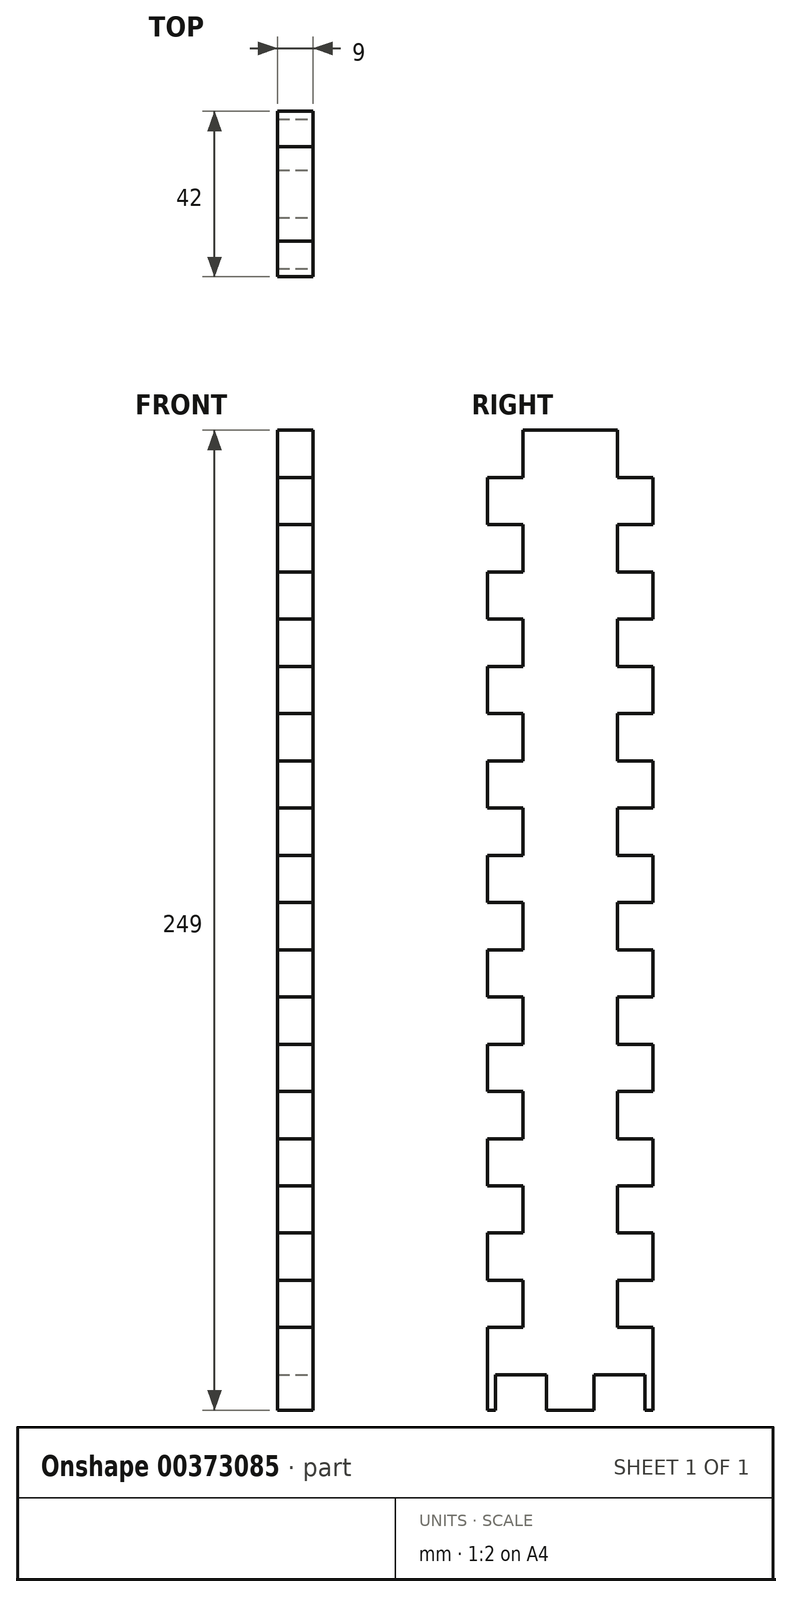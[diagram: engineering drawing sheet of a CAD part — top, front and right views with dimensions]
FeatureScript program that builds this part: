
annotation { "Feature Type Name" : "Feature", "Feature Type Description" : "" }
export const myFeature = defineFeature(function(context is Context, id is Id, definition is map)
    precondition{}
    {
        {
            var Q0;
            Q0=qCreatedBy(makeId("Right.planeOp"),FACE);
            var sketch = newSketch(context, id + "F0", { "sketchPlane" : qUnion([Q0])});
            skLineSegment(sketch, "E0.bottom", {"start": v(-12, 120) * mm, "end": v(12, 120) * mm});
            skLineSegment(sketch, "E0.top", {"start": v(-12, -120) * mm, "end": v(12, -120) * mm});
            skLineSegment(sketch, "E0.left", {"start": v(-12, 120) * mm, "end": v(-12, -120) * mm});
            skLineSegment(sketch, "E0.right", {"start": v(12, 120) * mm, "end": v(12, -120) * mm});
            skPoint(sketch, "E0.middle", {"position": v(0, 0) * mm});
            skSolve(sketch);
        }
        {
            var Q0;
            Q0=makeQuery(id+"F0.imprint","IMPRINT",FACE,{"disambiguationData":[TD([[makeQuery(id+"F0.imprint","IMPRINT",EDGE,{"derivedFrom":sQuery(id+"F0.wireOp",EDGE,"E0.bottom")}),-1.0]])]});
            extrude(context, id + "F1", {"entities" : qUnion([Q0]), "depth" : 9 * mm});
        }
        {
            var Q0;
            Q0=makeQuery(id+"F1.opExtrude","CAP_FACE",FACE,{"disambiguationData":[OSD([sQuery(id+"F0.wireOp",EDGE,"E0.bottom"),sQuery(id+"F0.wireOp",EDGE,"E0.top"),sQuery(id+"F0.wireOp",EDGE,"E0.left"),sQuery(id+"F0.wireOp",EDGE,"E0.right")])],"isStart":false});
            var sketch = newSketch(context, id + "F2", { "sketchPlane" : qUnion([Q0])});
            skLineSegment(sketch, "E1.bottom", {"start": v(-12, -120) * mm, "end": v(-21, -120) * mm});
            skLineSegment(sketch, "E1.top", {"start": v(-12, -108) * mm, "end": v(-21, -108) * mm});
            skLineSegment(sketch, "E1.left", {"start": v(-12, -120) * mm, "end": v(-12, -108) * mm});
            skLineSegment(sketch, "E1.right", {"start": v(-21, -120) * mm, "end": v(-21, -108) * mm});
            skLineSegment(sketch, "E2.0.1.0", {"start": v(-12, -84) * mm, "end": v(-21, -84) * mm});
            skLineSegment(sketch, "E2.0.1.1", {"start": v(-12, -96) * mm, "end": v(-12, -84) * mm});
            skLineSegment(sketch, "E2.0.1.2", {"start": v(-12, -96) * mm, "end": v(-21, -96) * mm});
            skLineSegment(sketch, "E2.0.1.3", {"start": v(-21, -96) * mm, "end": v(-21, -84) * mm});
            skLineSegment(sketch, "E2.0.2.0", {"start": v(-12, -60) * mm, "end": v(-21, -60) * mm});
            skLineSegment(sketch, "E2.0.2.1", {"start": v(-12, -72) * mm, "end": v(-12, -60) * mm});
            skLineSegment(sketch, "E2.0.2.2", {"start": v(-12, -72) * mm, "end": v(-21, -72) * mm});
            skLineSegment(sketch, "E2.0.2.3", {"start": v(-21, -72) * mm, "end": v(-21, -60) * mm});
            skLineSegment(sketch, "E2.0.3.0", {"start": v(-12, -36) * mm, "end": v(-21, -36) * mm});
            skLineSegment(sketch, "E2.0.3.1", {"start": v(-12, -48) * mm, "end": v(-12, -36) * mm});
            skLineSegment(sketch, "E2.0.3.2", {"start": v(-12, -48) * mm, "end": v(-21, -48) * mm});
            skLineSegment(sketch, "E2.0.3.3", {"start": v(-21, -48) * mm, "end": v(-21, -36) * mm});
            skLineSegment(sketch, "E2.0.4.0", {"start": v(-12, -12) * mm, "end": v(-21, -12) * mm});
            skLineSegment(sketch, "E2.0.4.1", {"start": v(-12, -24) * mm, "end": v(-12, -12) * mm});
            skLineSegment(sketch, "E2.0.4.2", {"start": v(-12, -24) * mm, "end": v(-21, -24) * mm});
            skLineSegment(sketch, "E2.0.4.3", {"start": v(-21, -24) * mm, "end": v(-21, -12) * mm});
            skLineSegment(sketch, "E2.0.5.0", {"start": v(-12, 12) * mm, "end": v(-21, 12) * mm});
            skLineSegment(sketch, "E2.0.5.1", {"start": v(-12, 0) * mm, "end": v(-12, 12) * mm});
            skLineSegment(sketch, "E2.0.5.2", {"start": v(-12, 0) * mm, "end": v(-21, 0) * mm});
            skLineSegment(sketch, "E2.0.5.3", {"start": v(-21, 0) * mm, "end": v(-21, 12) * mm});
            skLineSegment(sketch, "E2.0.6.0", {"start": v(-12, 36) * mm, "end": v(-21, 36) * mm});
            skLineSegment(sketch, "E2.0.6.1", {"start": v(-12, 24) * mm, "end": v(-12, 36) * mm});
            skLineSegment(sketch, "E2.0.6.2", {"start": v(-12, 24) * mm, "end": v(-21, 24) * mm});
            skLineSegment(sketch, "E2.0.6.3", {"start": v(-21, 24) * mm, "end": v(-21, 36) * mm});
            skLineSegment(sketch, "E2.0.7.0", {"start": v(-12, 60) * mm, "end": v(-21, 60) * mm});
            skLineSegment(sketch, "E2.0.7.1", {"start": v(-12, 48) * mm, "end": v(-12, 60) * mm});
            skLineSegment(sketch, "E2.0.7.2", {"start": v(-12, 48) * mm, "end": v(-21, 48) * mm});
            skLineSegment(sketch, "E2.0.7.3", {"start": v(-21, 48) * mm, "end": v(-21, 60) * mm});
            skLineSegment(sketch, "E2.0.8.0", {"start": v(-12, 84) * mm, "end": v(-21, 84) * mm});
            skLineSegment(sketch, "E2.0.8.1", {"start": v(-12, 72) * mm, "end": v(-12, 84) * mm});
            skLineSegment(sketch, "E2.0.8.2", {"start": v(-12, 72) * mm, "end": v(-21, 72) * mm});
            skLineSegment(sketch, "E2.0.8.3", {"start": v(-21, 72) * mm, "end": v(-21, 84) * mm});
            skLineSegment(sketch, "E2.0.9.0", {"start": v(-12, 108) * mm, "end": v(-21, 108) * mm});
            skLineSegment(sketch, "E2.0.9.1", {"start": v(-12, 96) * mm, "end": v(-12, 108) * mm});
            skLineSegment(sketch, "E2.0.9.2", {"start": v(-12, 96) * mm, "end": v(-21, 96) * mm});
            skLineSegment(sketch, "E2.0.9.3", {"start": v(-21, 96) * mm, "end": v(-21, 108) * mm});
            skLineSegment(sketch, "E2.direction1", {"start": v(-21, -108) * mm, "end": v(-11, -108) * mm, "construction": true});
            skLineSegment(sketch, "E2.direction2", {"start": v(-21, -108) * mm, "end": v(-21, -84) * mm, "construction": true});
            skLineSegment(sketch, "E3", {"start": v(0, 120) * mm, "end": v(0, 0) * mm});
            skLineSegment(sketch, "E4.MirrorCS", {"start": v(21, -96) * mm, "end": v(21, -84) * mm});
            skLineSegment(sketch, "E5.MirrorCS", {"start": v(21, 24) * mm, "end": v(21, 36) * mm});
            skLineSegment(sketch, "E6.MirrorCS", {"start": v(21, 96) * mm, "end": v(21, 108) * mm});
            skLineSegment(sketch, "E7.MirrorCS", {"start": v(21, -24) * mm, "end": v(21, -12) * mm});
            skLineSegment(sketch, "E8.MirrorCS", {"start": v(21, 72) * mm, "end": v(21, 84) * mm});
            skLineSegment(sketch, "E9.MirrorCS", {"start": v(12, 24) * mm, "end": v(21, 24) * mm});
            skLineSegment(sketch, "E10.MirrorCS", {"start": v(12, -24) * mm, "end": v(21, -24) * mm});
            skLineSegment(sketch, "E11.MirrorCS", {"start": v(12, 72) * mm, "end": v(21, 72) * mm});
            skLineSegment(sketch, "E12.MirrorCS", {"start": v(12, 0) * mm, "end": v(21, 0) * mm});
            skLineSegment(sketch, "E13.MirrorCS", {"start": v(21, 48) * mm, "end": v(21, 60) * mm});
            skLineSegment(sketch, "E14.MirrorCS", {"start": v(12, 96) * mm, "end": v(21, 96) * mm});
            skLineSegment(sketch, "E15.MirrorCS", {"start": v(12, -36) * mm, "end": v(21, -36) * mm});
            skLineSegment(sketch, "E16.MirrorCS", {"start": v(12, 24) * mm, "end": v(12, 36) * mm});
            skLineSegment(sketch, "E17.MirrorCS", {"start": v(21, -108) * mm, "end": v(21, -84) * mm, "construction": true});
            skLineSegment(sketch, "E18.MirrorCS", {"start": v(21, -72) * mm, "end": v(21, -60) * mm});
            skLineSegment(sketch, "E19.MirrorCS", {"start": v(12, -72) * mm, "end": v(21, -72) * mm});
            skLineSegment(sketch, "E20.MirrorCS", {"start": v(12, -72) * mm, "end": v(12, -60) * mm});
            skLineSegment(sketch, "E21.MirrorCS", {"start": v(12, -60) * mm, "end": v(21, -60) * mm});
            skLineSegment(sketch, "E22.MirrorCS", {"start": v(12, -96) * mm, "end": v(21, -96) * mm});
            skLineSegment(sketch, "E23.MirrorCS", {"start": v(12, -96) * mm, "end": v(12, -84) * mm});
            skLineSegment(sketch, "E24.MirrorCS", {"start": v(12, -84) * mm, "end": v(21, -84) * mm});
            skLineSegment(sketch, "E25.MirrorCS", {"start": v(21, -120) * mm, "end": v(21, -108) * mm});
            skLineSegment(sketch, "E26.MirrorCS", {"start": v(12, -120) * mm, "end": v(12, -108) * mm});
            skLineSegment(sketch, "E27.MirrorCS", {"start": v(12, -108) * mm, "end": v(21, -108) * mm});
            skLineSegment(sketch, "E28.MirrorCS", {"start": v(12, -120) * mm, "end": v(21, -120) * mm});
            skLineSegment(sketch, "E29.MirrorCS", {"start": v(21, -48) * mm, "end": v(21, -36) * mm});
            skLineSegment(sketch, "E30.MirrorCS", {"start": v(12, -48) * mm, "end": v(21, -48) * mm});
            skLineSegment(sketch, "E31.MirrorCS", {"start": v(12, -48) * mm, "end": v(12, -36) * mm});
            skLineSegment(sketch, "E32.MirrorCS", {"start": v(12, -24) * mm, "end": v(12, -12) * mm});
            skLineSegment(sketch, "E33.MirrorCS", {"start": v(12, 72) * mm, "end": v(12, 84) * mm});
            skLineSegment(sketch, "E34.MirrorCS", {"start": v(12, 0) * mm, "end": v(12, 12) * mm});
            skLineSegment(sketch, "E35.MirrorCS", {"start": v(12, 48) * mm, "end": v(21, 48) * mm});
            skLineSegment(sketch, "E36.MirrorCS", {"start": v(12, 96) * mm, "end": v(12, 108) * mm});
            skLineSegment(sketch, "E37.MirrorCS", {"start": v(12, 36) * mm, "end": v(21, 36) * mm});
            skLineSegment(sketch, "E38.MirrorCS", {"start": v(12, 60) * mm, "end": v(21, 60) * mm});
            skLineSegment(sketch, "E39.MirrorCS", {"start": v(12, -12) * mm, "end": v(21, -12) * mm});
            skLineSegment(sketch, "E40.MirrorCS", {"start": v(12, 108) * mm, "end": v(21, 108) * mm});
            skLineSegment(sketch, "E41.MirrorCS", {"start": v(12, 48) * mm, "end": v(12, 60) * mm});
            skLineSegment(sketch, "E42.MirrorCS", {"start": v(12, 12) * mm, "end": v(21, 12) * mm});
            skLineSegment(sketch, "E43.MirrorCS", {"start": v(12, 84) * mm, "end": v(21, 84) * mm});
            skLineSegment(sketch, "E44.MirrorCS", {"start": v(21, 0) * mm, "end": v(21, 12) * mm});
            skSolve(sketch);
        }
        {
            var Q0;
            Q0 = qSketchRegion(id + "F2", true);
            var Q1;
            Q1=makeQuery(id+"F1.opExtrude","CAP_FACE",FACE,{"disambiguationData":[OSD([sQuery(id+"F0.wireOp",EDGE,"E0.bottom"),sQuery(id+"F0.wireOp",EDGE,"E0.top"),sQuery(id+"F0.wireOp",EDGE,"E0.left"),sQuery(id+"F0.wireOp",EDGE,"E0.right")])],"isStart":true});
            extrude(context, id + "F3", {"entities" : qUnion([Q0]), "operationType" : NewBodyOperationType.ADD, "endBound" : BoundingType.UP_TO_SURFACE, "oppositeDirection" : true, "endBoundEntityFace" : qUnion([Q1]), "depth" : 25 * mm});
        }
        {
            var Q0;
            Q0=makeQuery(id+"F3.boolean.opBoolean","MERGE",FACE,{"derivedFrom":[makeQuery(id+"F1.opExtrude","CAP_FACE",FACE,{"disambiguationData":[OSD([sQuery(id+"F0.wireOp",EDGE,"E0.bottom"),sQuery(id+"F0.wireOp",EDGE,"E0.top"),sQuery(id+"F0.wireOp",EDGE,"E0.left"),sQuery(id+"F0.wireOp",EDGE,"E0.right")])],"isStart":false}),makeQuery(id+"F3.opExtrude","CAP_FACE",FACE,{"disambiguationData":[OSD([sQuery(id+"F2.wireOp",EDGE,"E1.bottom"),sQuery(id+"F2.wireOp",EDGE,"E1.top"),sQuery(id+"F2.wireOp",EDGE,"E1.left"),sQuery(id+"F2.wireOp",EDGE,"E1.right")])],"isStart":true}),makeQuery(id+"F3.opExtrude","CAP_FACE",FACE,{"disambiguationData":[OSD([sQuery(id+"F2.wireOp",EDGE,"E2.0.1.0"),sQuery(id+"F2.wireOp",EDGE,"E2.0.1.1"),sQuery(id+"F2.wireOp",EDGE,"E2.0.1.2"),sQuery(id+"F2.wireOp",EDGE,"E2.0.1.3")])],"isStart":true}),makeQuery(id+"F3.opExtrude","CAP_FACE",FACE,{"disambiguationData":[OSD([sQuery(id+"F2.wireOp",EDGE,"E2.0.2.0"),sQuery(id+"F2.wireOp",EDGE,"E2.0.2.1"),sQuery(id+"F2.wireOp",EDGE,"E2.0.2.2"),sQuery(id+"F2.wireOp",EDGE,"E2.0.2.3")])],"isStart":true}),makeQuery(id+"F3.opExtrude","CAP_FACE",FACE,{"disambiguationData":[OSD([sQuery(id+"F2.wireOp",EDGE,"E2.0.3.0"),sQuery(id+"F2.wireOp",EDGE,"E2.0.3.1"),sQuery(id+"F2.wireOp",EDGE,"E2.0.3.2"),sQuery(id+"F2.wireOp",EDGE,"E2.0.3.3")])],"isStart":true}),makeQuery(id+"F3.opExtrude","CAP_FACE",FACE,{"disambiguationData":[OSD([sQuery(id+"F2.wireOp",EDGE,"E2.0.4.0"),sQuery(id+"F2.wireOp",EDGE,"E2.0.4.1"),sQuery(id+"F2.wireOp",EDGE,"E2.0.4.2"),sQuery(id+"F2.wireOp",EDGE,"E2.0.4.3")])],"isStart":true}),makeQuery(id+"F3.opExtrude","CAP_FACE",FACE,{"disambiguationData":[OSD([sQuery(id+"F2.wireOp",EDGE,"E2.0.5.0"),sQuery(id+"F2.wireOp",EDGE,"E2.0.5.1"),sQuery(id+"F2.wireOp",EDGE,"E2.0.5.2"),sQuery(id+"F2.wireOp",EDGE,"E2.0.5.3")])],"isStart":true}),makeQuery(id+"F3.opExtrude","CAP_FACE",FACE,{"disambiguationData":[OSD([sQuery(id+"F2.wireOp",EDGE,"E2.0.6.0"),sQuery(id+"F2.wireOp",EDGE,"E2.0.6.1"),sQuery(id+"F2.wireOp",EDGE,"E2.0.6.2"),sQuery(id+"F2.wireOp",EDGE,"E2.0.6.3")])],"isStart":true}),makeQuery(id+"F3.opExtrude","CAP_FACE",FACE,{"disambiguationData":[OSD([sQuery(id+"F2.wireOp",EDGE,"E2.0.7.0"),sQuery(id+"F2.wireOp",EDGE,"E2.0.7.1"),sQuery(id+"F2.wireOp",EDGE,"E2.0.7.2"),sQuery(id+"F2.wireOp",EDGE,"E2.0.7.3")])],"isStart":true}),makeQuery(id+"F3.opExtrude","CAP_FACE",FACE,{"disambiguationData":[OSD([sQuery(id+"F2.wireOp",EDGE,"E2.0.8.0"),sQuery(id+"F2.wireOp",EDGE,"E2.0.8.1"),sQuery(id+"F2.wireOp",EDGE,"E2.0.8.2"),sQuery(id+"F2.wireOp",EDGE,"E2.0.8.3")])],"isStart":true}),makeQuery(id+"F3.opExtrude","CAP_FACE",FACE,{"disambiguationData":[OSD([sQuery(id+"F2.wireOp",EDGE,"E2.0.9.0"),sQuery(id+"F2.wireOp",EDGE,"E2.0.9.1"),sQuery(id+"F2.wireOp",EDGE,"E2.0.9.2"),sQuery(id+"F2.wireOp",EDGE,"E2.0.9.3")])],"isStart":true}),makeQuery(id+"F3.opExtrude","CAP_FACE",FACE,{"disambiguationData":[OSD([sQuery(id+"F2.wireOp",EDGE,"E4.MirrorCS"),sQuery(id+"F2.wireOp",EDGE,"E22.MirrorCS"),sQuery(id+"F2.wireOp",EDGE,"E23.MirrorCS"),sQuery(id+"F2.wireOp",EDGE,"E24.MirrorCS")])],"isStart":true}),makeQuery(id+"F3.opExtrude","CAP_FACE",FACE,{"disambiguationData":[OSD([sQuery(id+"F2.wireOp",EDGE,"E5.MirrorCS"),sQuery(id+"F2.wireOp",EDGE,"E9.MirrorCS"),sQuery(id+"F2.wireOp",EDGE,"E16.MirrorCS"),sQuery(id+"F2.wireOp",EDGE,"E37.MirrorCS")])],"isStart":true}),makeQuery(id+"F3.opExtrude","CAP_FACE",FACE,{"disambiguationData":[OSD([sQuery(id+"F2.wireOp",EDGE,"E6.MirrorCS"),sQuery(id+"F2.wireOp",EDGE,"E14.MirrorCS"),sQuery(id+"F2.wireOp",EDGE,"E36.MirrorCS"),sQuery(id+"F2.wireOp",EDGE,"E40.MirrorCS")])],"isStart":true}),makeQuery(id+"F3.opExtrude","CAP_FACE",FACE,{"disambiguationData":[OSD([sQuery(id+"F2.wireOp",EDGE,"E7.MirrorCS"),sQuery(id+"F2.wireOp",EDGE,"E10.MirrorCS"),sQuery(id+"F2.wireOp",EDGE,"E32.MirrorCS"),sQuery(id+"F2.wireOp",EDGE,"E39.MirrorCS")])],"isStart":true}),makeQuery(id+"F3.opExtrude","CAP_FACE",FACE,{"disambiguationData":[OSD([sQuery(id+"F2.wireOp",EDGE,"E8.MirrorCS"),sQuery(id+"F2.wireOp",EDGE,"E11.MirrorCS"),sQuery(id+"F2.wireOp",EDGE,"E33.MirrorCS"),sQuery(id+"F2.wireOp",EDGE,"E43.MirrorCS")])],"isStart":true}),makeQuery(id+"F3.opExtrude","CAP_FACE",FACE,{"disambiguationData":[OSD([sQuery(id+"F2.wireOp",EDGE,"E12.MirrorCS"),sQuery(id+"F2.wireOp",EDGE,"E34.MirrorCS"),sQuery(id+"F2.wireOp",EDGE,"E42.MirrorCS"),sQuery(id+"F2.wireOp",EDGE,"E44.MirrorCS")])],"isStart":true}),makeQuery(id+"F3.opExtrude","CAP_FACE",FACE,{"disambiguationData":[OSD([sQuery(id+"F2.wireOp",EDGE,"E13.MirrorCS"),sQuery(id+"F2.wireOp",EDGE,"E35.MirrorCS"),sQuery(id+"F2.wireOp",EDGE,"E38.MirrorCS"),sQuery(id+"F2.wireOp",EDGE,"E41.MirrorCS")])],"isStart":true}),makeQuery(id+"F3.opExtrude","CAP_FACE",FACE,{"disambiguationData":[OSD([sQuery(id+"F2.wireOp",EDGE,"E15.MirrorCS"),sQuery(id+"F2.wireOp",EDGE,"E29.MirrorCS"),sQuery(id+"F2.wireOp",EDGE,"E30.MirrorCS"),sQuery(id+"F2.wireOp",EDGE,"E31.MirrorCS")])],"isStart":true}),makeQuery(id+"F3.opExtrude","CAP_FACE",FACE,{"disambiguationData":[OSD([sQuery(id+"F2.wireOp",EDGE,"E18.MirrorCS"),sQuery(id+"F2.wireOp",EDGE,"E19.MirrorCS"),sQuery(id+"F2.wireOp",EDGE,"E20.MirrorCS"),sQuery(id+"F2.wireOp",EDGE,"E21.MirrorCS")])],"isStart":true}),makeQuery(id+"F3.opExtrude","CAP_FACE",FACE,{"disambiguationData":[OSD([sQuery(id+"F2.wireOp",EDGE,"E25.MirrorCS"),sQuery(id+"F2.wireOp",EDGE,"E26.MirrorCS"),sQuery(id+"F2.wireOp",EDGE,"E27.MirrorCS"),sQuery(id+"F2.wireOp",EDGE,"E28.MirrorCS")])],"isStart":true})]});
            var sketch = newSketch(context, id + "F4", { "sketchPlane" : qUnion([Q0])});
            skLineSegment(sketch, "E45", {"start": v(0, -120) * mm, "end": v(0, -124.5) * mm, "construction": true});
            skLineSegment(sketch, "E46.bottom", {"start": v(6, -120) * mm, "end": v(-6, -120) * mm});
            skLineSegment(sketch, "E46.top", {"start": v(6, -129) * mm, "end": v(-6, -129) * mm});
            skLineSegment(sketch, "E46.left", {"start": v(6, -120) * mm, "end": v(6, -129) * mm});
            skLineSegment(sketch, "E46.right", {"start": v(-6, -120) * mm, "end": v(-6, -129) * mm});
            skPoint(sketch, "E46.middle", {"position": v(0, -124.5) * mm});
            skLineSegment(sketch, "E47.1.0.1", {"start": v(21, -120) * mm, "end": v(19, -120) * mm});
            skLineSegment(sketch, "E47.1.0.2", {"start": v(19, -120) * mm, "end": v(19, -129) * mm});
            skLineSegment(sketch, "E47.1.0.3", {"start": v(21, -129) * mm, "end": v(19, -129) * mm});
            skLineSegment(sketch, "E47.direction1", {"start": v(6, -129) * mm, "end": v(21, -129) * mm, "construction": true});
            skLineSegment(sketch, "E48.MirrorCS", {"start": v(-19, -120) * mm, "end": v(-19, -129) * mm});
            skPoint(sketch, "E49.MirrorCS.start.orphan", {"position": v(19, -138) * mm});
            skPoint(sketch, "E50.MirrorCS.start.orphan", {"position": v(31, -138) * mm});
            skLineSegment(sketch, "E51", {"start": v(-21, -129) * mm, "end": v(-19, -129) * mm});
            skLineSegment(sketch, "E52", {"start": v(-21, -120) * mm, "end": v(-21, -129) * mm});
            skPoint(sketch, "E53.MirrorCS.start.orphan", {"position": v(-31, -120) * mm});
            skPoint(sketch, "E54.orphan", {"position": v(-31, -129) * mm});
            skLineSegment(sketch, "E55", {"start": v(21, -120) * mm, "end": v(21, -129) * mm});
            skPoint(sketch, "E56.orphan", {"position": v(31, -120) * mm});
            skPoint(sketch, "E57.orphan", {"position": v(31, -129) * mm});
            skLineSegment(sketch, "E58", {"start": v(-21, -120) * mm, "end": v(-19, -120) * mm});
            skSolve(sketch);
        }
        {
            var Q0;
            Q0 = qSketchRegion(id + "F4", true);
            var Q1;
            {var subQ0=sQuery(id+"F0.wireOp",EDGE,"E0.right");var subQ1=sQuery(id+"F0.wireOp",EDGE,"E0.left");var subQ2=sQuery(id+"F0.wireOp",EDGE,"E0.top");var subQ3=sQuery(id+"F0.wireOp",EDGE,"E0.bottom");Q1=makeQuery(id+"F3.boolean.opBoolean","MERGE",FACE,{"derivedFrom":[makeQuery(id+"F1.opExtrude","CAP_FACE",FACE,{"disambiguationData":[OSD([subQ3,subQ2,subQ1,subQ0])],"isStart":true}),makeQuery(id+"F3.opExtrude","CAP_FACE",FACE,{"disambiguationData":[OSD([subQ3,subQ2,subQ1,subQ0]),ownerDisambiguation([makeQuery(id+"F2.imprint","IMPRINT",EDGE,{"derivedFrom":sQuery(id+"F2.wireOp",EDGE,"E1.bottom")})])],"isStart":false}),makeQuery(id+"F3.opExtrude","CAP_FACE",FACE,{"disambiguationData":[OSD([subQ3,subQ2,subQ1,subQ0]),ownerDisambiguation([makeQuery(id+"F2.imprint","IMPRINT",EDGE,{"derivedFrom":sQuery(id+"F2.wireOp",EDGE,"E2.0.1.0")})])],"isStart":false}),makeQuery(id+"F3.opExtrude","CAP_FACE",FACE,{"disambiguationData":[OSD([subQ3,subQ2,subQ1,subQ0]),ownerDisambiguation([makeQuery(id+"F2.imprint","IMPRINT",EDGE,{"derivedFrom":sQuery(id+"F2.wireOp",EDGE,"E2.0.2.0")})])],"isStart":false}),makeQuery(id+"F3.opExtrude","CAP_FACE",FACE,{"disambiguationData":[OSD([subQ3,subQ2,subQ1,subQ0]),ownerDisambiguation([makeQuery(id+"F2.imprint","IMPRINT",EDGE,{"derivedFrom":sQuery(id+"F2.wireOp",EDGE,"E2.0.3.0")})])],"isStart":false}),makeQuery(id+"F3.opExtrude","CAP_FACE",FACE,{"disambiguationData":[OSD([subQ3,subQ2,subQ1,subQ0]),ownerDisambiguation([makeQuery(id+"F2.imprint","IMPRINT",EDGE,{"derivedFrom":sQuery(id+"F2.wireOp",EDGE,"E2.0.4.0")})])],"isStart":false}),makeQuery(id+"F3.opExtrude","CAP_FACE",FACE,{"disambiguationData":[OSD([subQ3,subQ2,subQ1,subQ0]),ownerDisambiguation([makeQuery(id+"F2.imprint","IMPRINT",EDGE,{"derivedFrom":sQuery(id+"F2.wireOp",EDGE,"E2.0.5.0")})])],"isStart":false}),makeQuery(id+"F3.opExtrude","CAP_FACE",FACE,{"disambiguationData":[OSD([subQ3,subQ2,subQ1,subQ0]),ownerDisambiguation([makeQuery(id+"F2.imprint","IMPRINT",EDGE,{"derivedFrom":sQuery(id+"F2.wireOp",EDGE,"E2.0.6.0")})])],"isStart":false}),makeQuery(id+"F3.opExtrude","CAP_FACE",FACE,{"disambiguationData":[OSD([subQ3,subQ2,subQ1,subQ0]),ownerDisambiguation([makeQuery(id+"F2.imprint","IMPRINT",EDGE,{"derivedFrom":sQuery(id+"F2.wireOp",EDGE,"E2.0.7.0")})])],"isStart":false}),makeQuery(id+"F3.opExtrude","CAP_FACE",FACE,{"disambiguationData":[OSD([subQ3,subQ2,subQ1,subQ0]),ownerDisambiguation([makeQuery(id+"F2.imprint","IMPRINT",EDGE,{"derivedFrom":sQuery(id+"F2.wireOp",EDGE,"E2.0.8.0")})])],"isStart":false}),makeQuery(id+"F3.opExtrude","CAP_FACE",FACE,{"disambiguationData":[OSD([subQ3,subQ2,subQ1,subQ0]),ownerDisambiguation([makeQuery(id+"F2.imprint","IMPRINT",EDGE,{"derivedFrom":sQuery(id+"F2.wireOp",EDGE,"E2.0.9.0")})])],"isStart":false}),makeQuery(id+"F3.opExtrude","CAP_FACE",FACE,{"disambiguationData":[OSD([subQ3,subQ2,subQ1,subQ0]),ownerDisambiguation([makeQuery(id+"F2.imprint","IMPRINT",EDGE,{"derivedFrom":sQuery(id+"F2.wireOp",EDGE,"E4.MirrorCS")})])],"isStart":false}),makeQuery(id+"F3.opExtrude","CAP_FACE",FACE,{"disambiguationData":[OSD([subQ3,subQ2,subQ1,subQ0]),ownerDisambiguation([makeQuery(id+"F2.imprint","IMPRINT",EDGE,{"derivedFrom":sQuery(id+"F2.wireOp",EDGE,"E5.MirrorCS")})])],"isStart":false}),makeQuery(id+"F3.opExtrude","CAP_FACE",FACE,{"disambiguationData":[OSD([subQ3,subQ2,subQ1,subQ0]),ownerDisambiguation([makeQuery(id+"F2.imprint","IMPRINT",EDGE,{"derivedFrom":sQuery(id+"F2.wireOp",EDGE,"E6.MirrorCS")})])],"isStart":false}),makeQuery(id+"F3.opExtrude","CAP_FACE",FACE,{"disambiguationData":[OSD([subQ3,subQ2,subQ1,subQ0]),ownerDisambiguation([makeQuery(id+"F2.imprint","IMPRINT",EDGE,{"derivedFrom":sQuery(id+"F2.wireOp",EDGE,"E7.MirrorCS")})])],"isStart":false}),makeQuery(id+"F3.opExtrude","CAP_FACE",FACE,{"disambiguationData":[OSD([subQ3,subQ2,subQ1,subQ0]),ownerDisambiguation([makeQuery(id+"F2.imprint","IMPRINT",EDGE,{"derivedFrom":sQuery(id+"F2.wireOp",EDGE,"E8.MirrorCS")})])],"isStart":false}),makeQuery(id+"F3.opExtrude","CAP_FACE",FACE,{"disambiguationData":[OSD([subQ3,subQ2,subQ1,subQ0]),ownerDisambiguation([makeQuery(id+"F2.imprint","IMPRINT",EDGE,{"derivedFrom":sQuery(id+"F2.wireOp",EDGE,"E12.MirrorCS")})])],"isStart":false}),makeQuery(id+"F3.opExtrude","CAP_FACE",FACE,{"disambiguationData":[OSD([subQ3,subQ2,subQ1,subQ0]),ownerDisambiguation([makeQuery(id+"F2.imprint","IMPRINT",EDGE,{"derivedFrom":sQuery(id+"F2.wireOp",EDGE,"E13.MirrorCS")})])],"isStart":false}),makeQuery(id+"F3.opExtrude","CAP_FACE",FACE,{"disambiguationData":[OSD([subQ3,subQ2,subQ1,subQ0]),ownerDisambiguation([makeQuery(id+"F2.imprint","IMPRINT",EDGE,{"derivedFrom":sQuery(id+"F2.wireOp",EDGE,"E15.MirrorCS")})])],"isStart":false}),makeQuery(id+"F3.opExtrude","CAP_FACE",FACE,{"disambiguationData":[OSD([subQ3,subQ2,subQ1,subQ0]),ownerDisambiguation([makeQuery(id+"F2.imprint","IMPRINT",EDGE,{"derivedFrom":sQuery(id+"F2.wireOp",EDGE,"E18.MirrorCS")})])],"isStart":false}),makeQuery(id+"F3.opExtrude","CAP_FACE",FACE,{"disambiguationData":[OSD([subQ3,subQ2,subQ1,subQ0]),ownerDisambiguation([makeQuery(id+"F2.imprint","IMPRINT",EDGE,{"derivedFrom":sQuery(id+"F2.wireOp",EDGE,"E25.MirrorCS")})])],"isStart":false})]});}
            extrude(context, id + "F5", {"entities" : qUnion([Q0]), "operationType" : NewBodyOperationType.ADD, "endBound" : BoundingType.UP_TO_SURFACE, "oppositeDirection" : true, "endBoundEntityFace" : qUnion([Q1]), "depth" : 25 * mm});
        }
    });
